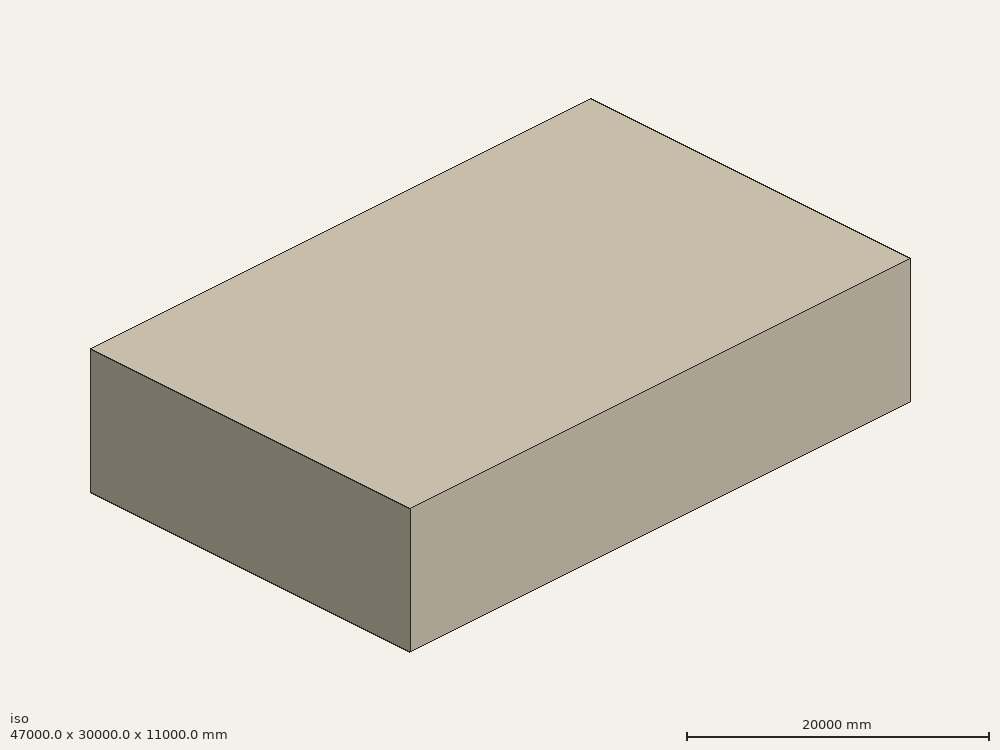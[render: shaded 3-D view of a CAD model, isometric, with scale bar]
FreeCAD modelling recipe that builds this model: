
FCSTD DOCUMENT  (FreeCAD 0.20R29603 (Git))
Label: windforces_cfMesh_panels_alogne
License: All rights reserved
LicenseURL: http://en.wikipedia.org/wiki/All_rights_reserved
objects: Part::FeaturePython×8, Part::Feature×4, Part::Box×3, App::DocumentObjectGroupPython×2, Mesh::Feature×1, Part::MultiFuse×1, Part::Cut×1, App::MaterialObjectPython×1
note: 17 computed .brp shape members not serialized (recipe doc carries the construction recipe); baked Part::Feature solids carry a one-line shape summary decoded from their .brp

FEATURE [Mesh::Feature] cfdwindforce
FEATURE [Part::Feature] cfdwindforce001
  shape: bbox 15090 x 17300 x 3871 mm, 94 faces, 0 solids (baked)
FEATURE [Part::Feature] cfdwindforce001_solid  label="cfdwindforce001 (Solid)"
  Placement = pos=(-7500,-8500,0) rot=(0,0,1;0rad)
  shape: bbox 15090 x 17300 x 3871 mm, 94 faces (baked)
FEATURE [Part::Box] Box  label="Cube"
  AttacherType = Attacher::AttachEngine3D
  Height = 11000
  Length = 47000
  Placement = pos=(-22000,-14000,-1000) rot=(0,0,1;0rad)
  Width = 30000
FEATURE [Part::Box] Box001  label="Cube001"
  AttacherType = Attacher::AttachEngine3D
  Height = 1400
  Length = 70
  Placement = pos=(4750,-7000,4000) rot=(0,1,0;1.0472rad)
  Width = 15000
FEATURE [Part::Feature] Box001001  label="Cube002"
  Placement = pos=(250,-7000,4000) rot=(0,1,0;1.0472rad)
  shape: bbox 1247 x 15000 x 760.6 mm, 6 faces (baked)
FEATURE [Part::Feature] Box001002  label="Cube003"
  Placement = pos=(2500,-7000,4000) rot=(0,1,0;1.0472rad)
  shape: bbox 1247 x 15000 x 760.6 mm, 6 faces (baked)
FEATURE [Part::Box] Box001003  label="refinement"
  AttacherType = Attacher::AttachEngine3D
  Height = 3000
  Length = 8000
  Placement = pos=(-1000,-8000,3000) rot=(0,0,1;0rad)
  Width = 17000
FEATURE [Part::MultiFuse] Fusion  label="panels"
  Shapes = -> [Box001,Box001001,Box001002]
FEATURE [Part::Cut] Cut  label="panels_model"
  Base = -> Box
  Tool = -> Fusion
FEATURE [Part::FeaturePython] PhysicsModel  # WARN: FeaturePython — macro-defined, semantics opaque (R4)
  Flow = 0
  Phase = 0
  SRFModelAxis = (0,0,0)
  SRFModelCoR = (0,0,0)
  SRFModelEnabled = false
  SRFModelRPM = 0
  Time = 0
  Turbulence = 3
  TurbulenceModel = 0
  gx = 0
  gy = -9800
  gz = 0
FEATURE [App::MaterialObjectPython] FluidProperties  # material (typed FeaturePython)
  Category = 1
  Material = CardName=AirIsothermal; Density=1.20 kg/m^3; Description=Standard air properties at 20 Degrees Celsius and 1 atm; DynamicViscosity=1.80e-5 kg/m/s; Name=Air; Type=Isothermal
FEATURE [Part::FeaturePython] InitialiseFields  # WARN: FeaturePython — macro-defined, semantics opaque (R4)
  PotentialFlow = true
  PotentialFlowP = true
  Pressure = 100
  ReThetat = 1
  Temperature = 290
  UseInletTemperatureValue = false
  UseInletTurbulenceValues = false
  UseInletUValues = false
  UseOutletPValue = false
  Ux = 0
  Uy = 0
  Uz = 0
  epsilon = 50000000
  gammaInt = 1
  k = 10000
  nuTilda = 55000000
  nut = 50000000
  omega = 1
FEATURE [Part::FeaturePython] CfdSolver  # WARN: FeaturePython — macro-defined, semantics opaque (R4)
  ConvergenceTol = 0.001
  EndTime = 1
  InputCaseName = case
  MaxCFLNumber = 5
  MaxInterfaceCFLNumber = 5
  MaxIterations = 2000
  Parallel = true
  ParallelCores = 4
  PurgeWrite = 0
  StartFrom = 0
  SteadyWriteInterval = 100
  TimeStep = 0.001
  TransientWriteInterval = 0.1
FEATURE [Part::FeaturePython] MeshRefinement  # WARN: FeaturePython — macro-defined, semantics opaque (R4)
  ExpansionRatio = 1
  Extrusion = false
  ExtrusionAngle = 5
  ExtrusionAxisDirection = (1,0,0)
  ExtrusionAxisPoint = (0,0,0)
  ExtrusionLayers = 1
  ExtrusionRatio = 1
  ExtrusionThickness = 1
  ExtrusionType = 2DPlanar
  FirstLayerHeight = 0
  Internal = true
  KeepExistingMesh = false
  NumberLayers = 0
  RefinementThickness = 0
  RegionEdgeRefinement = 1
  RelativeLength = 0.5
FEATURE [Part::FeaturePython] MeshRefinement001  # WARN: FeaturePython — macro-defined, semantics opaque (R4)
  ExpansionRatio = 1
  Extrusion = false
  ExtrusionAngle = 5
  ExtrusionAxisDirection = (1,0,0)
  ExtrusionAxisPoint = (0,0,0)
  ExtrusionLayers = 1
  ExtrusionRatio = 1
  ExtrusionThickness = 1
  ExtrusionType = 2DPlanar
  FirstLayerHeight = 0
  Internal = false
  KeepExistingMesh = false
  NumberLayers = 5
  RefinementThickness = 0
  RegionEdgeRefinement = 1
  RelativeLength = 0.25
  ShapeRefs = -> [Cut]
FEATURE [App::DocumentObjectGroupPython] Cut_Mesh  # scripted group (container) (typed FeaturePython)
  CaseName = meshCase
  CellsBetweenLevels = 3
  CharacteristicLengthMax = 1000
  ConvertToDualMesh = false
  EdgeRefinement = 1
  ElementDimension = 1
  Group = -> [MeshRefinement,MeshRefinement001]
  ImplicitEdgeDetection = false
  MeshUtility = 0
  NumberOfProcesses = 1
  NumberOfThreads = 0
  Part = -> Cut
  PointInMesh = x=0 m; y=0 m; z=0 m
  STLAngularMeshDensity = 100
  STLRelativeLinearDeflection = 0.001
FEATURE [Part::FeaturePython] CfdFluidBoundary  label="inlet"  # WARN: FeaturePython — macro-defined, semantics opaque (R4)
  BoundarySubType = 5
  BoundaryType = 1
  DefaultBoundary = false
  DissipationRate = 50000000
  HeatFlux = 0
  HeatTransferCoeff = 0
  Intermittency = 1
  MassFlowRate = 0
  NuTilda = 55000000
  PeriodicCentreOfRotation = (0,0,0)
  PeriodicCentreOfRotationAxis = (0,0,0)
  PeriodicMaster = true
  PeriodicSeparationVector = (0,0,0)
  PorousBaffleMethod = 0
  Pressure = 100
  PressureDropCoeff = 0
  ReThetat = 1
  RelativeToFrame = false
  ReverseNormal = false
  RotationalPeriodic = false
  RoughnessConstant = 0.5
  RoughnessHeight = 0
  ScreenSpacing = 2
  ScreenWireDiameter = 0.2
  ShapeRefs = -> [Cut]
  SlipRatio = 0
  SpecificDissipationRate = 1
  Temperature = 290
  ThermalBoundaryType = 0
  TurbulenceInletSpecification = 0
  TurbulenceIntensityPercentage = 1
  TurbulenceLengthScale = 100
  TurbulentKineticEnergy = 10000
  TurbulentViscosity = 50000000
  Ux = -10
  Uy = 0
  Uz = 0
  VelocityIsCartesian = true
  VelocityMag = 0
  VolFlowRate = 0
  kEqnTurbulentKineticEnergy = 10000
  kEqnTurbulentViscosity = 50000000
FEATURE [Part::FeaturePython] CfdFluidBoundary001  label="open"  # WARN: FeaturePython — macro-defined, semantics opaque (R4)
  BoundarySubType = 13
  BoundaryType = 3
  DefaultBoundary = false
  DissipationRate = 50000000
  HeatFlux = 0
  HeatTransferCoeff = 0
  Intermittency = 1
  MassFlowRate = 0
  NuTilda = 55000000
  PeriodicCentreOfRotation = (0,0,0)
  PeriodicCentreOfRotationAxis = (0,0,0)
  PeriodicMaster = true
  PeriodicSeparationVector = (0,0,0)
  PorousBaffleMethod = 0
  Pressure = 100
  PressureDropCoeff = 0
  ReThetat = 1
  RelativeToFrame = false
  ReverseNormal = false
  RotationalPeriodic = false
  RoughnessConstant = 0.5
  RoughnessHeight = 0
  ScreenSpacing = 2
  ScreenWireDiameter = 0.2
  ShapeRefs = -> [Cut]
  SlipRatio = 0
  SpecificDissipationRate = 1
  Temperature = 290
  ThermalBoundaryType = 0
  TurbulenceInletSpecification = 0
  TurbulenceIntensityPercentage = 1
  TurbulenceLengthScale = 100
  TurbulentKineticEnergy = 10000
  TurbulentViscosity = 50000000
  Ux = 0
  Uy = 0
  Uz = 0
  VelocityIsCartesian = true
  VelocityMag = 0
  VolFlowRate = 0
  kEqnTurbulentKineticEnergy = 10000
  kEqnTurbulentViscosity = 50000000
FEATURE [Part::FeaturePython] CfdFluidBoundary002  label="wall"  # WARN: FeaturePython — macro-defined, semantics opaque (R4)
  BoundarySubType = 0
  BoundaryType = 0
  DefaultBoundary = false
  DissipationRate = 50000000
  HeatFlux = 0
  HeatTransferCoeff = 0
  Intermittency = 1
  MassFlowRate = 0
  NuTilda = 55000000
  PeriodicCentreOfRotation = (0,0,0)
  PeriodicCentreOfRotationAxis = (0,0,0)
  PeriodicMaster = true
  PeriodicSeparationVector = (0,0,0)
  PorousBaffleMethod = 0
  Pressure = 100
  PressureDropCoeff = 0
  ReThetat = 1
  RelativeToFrame = false
  ReverseNormal = false
  RotationalPeriodic = false
  RoughnessConstant = 0.5
  RoughnessHeight = 0
  ScreenSpacing = 2
  ScreenWireDiameter = 0.2
  ShapeRefs = -> [Cut]
  SlipRatio = 0
  SpecificDissipationRate = 1
  Temperature = 290
  ThermalBoundaryType = 0
  TurbulenceInletSpecification = 0
  TurbulenceIntensityPercentage = 1
  TurbulenceLengthScale = 100
  TurbulentKineticEnergy = 10000
  TurbulentViscosity = 50000000
  Ux = 0
  Uy = 0
  Uz = 0
  VelocityIsCartesian = true
  VelocityMag = 0
  VolFlowRate = 0
  kEqnTurbulentKineticEnergy = 10000
  kEqnTurbulentViscosity = 50000000
FEATURE [App::DocumentObjectGroupPython] CfdAnalysis  # scripted group (container) (typed FeaturePython)
  Group = -> [PhysicsModel,FluidProperties,InitialiseFields,CfdSolver,Cut_Mesh,CfdFluidBoundary,CfdFluidBoundary001,CfdFluidBoundary002]
  IsActiveAnalysis = true
  NeedsCaseRewrite = false
  NeedsMeshRerun = false
  NeedsMeshRewrite = false
